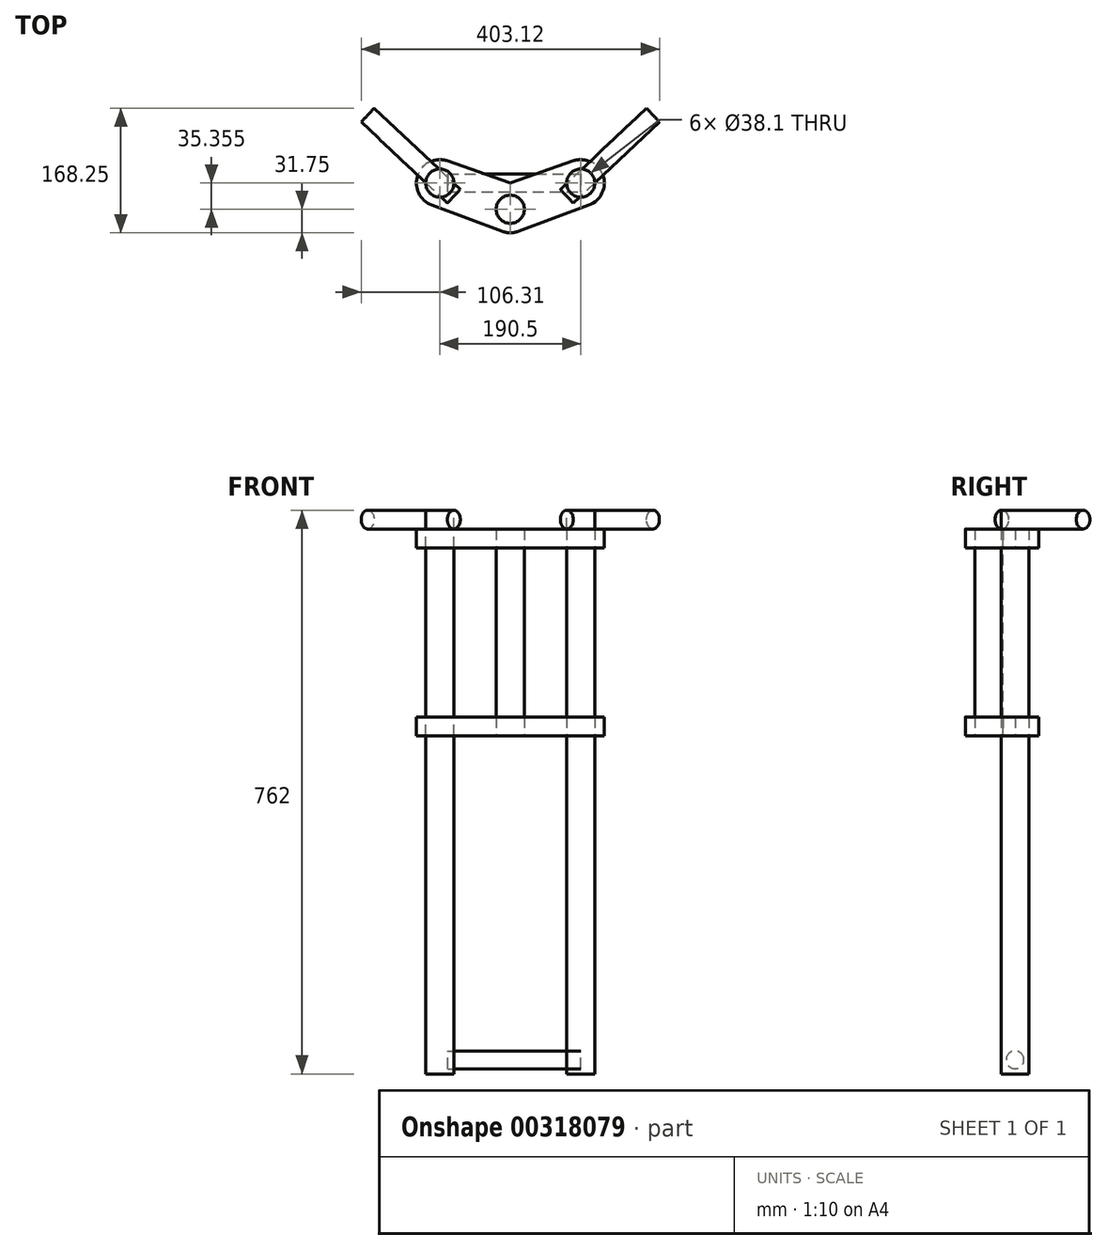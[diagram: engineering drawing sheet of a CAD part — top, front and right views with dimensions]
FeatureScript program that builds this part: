
annotation { "Feature Type Name" : "Feature", "Feature Type Description" : "" }
export const myFeature = defineFeature(function(context is Context, id is Id, definition is map)
    precondition{}
    {
        {
            var Q0;
            Q0=qCreatedBy(makeId("Top.planeOp"),FACE);
            var sketch = newSketch(context, id + "F0", { "sketchPlane" : qUnion([Q0])});
            skCircle(sketch, "E0", {"center": v(0, 0) * mm, "radius": 19.05 * mm});
            skCircle(sketch, "E1", {"center": v(-95.25, 35.36) * mm, "radius": 19.05 * mm});
            skCircle(sketch, "E2", {"center": v(95.25, 35.36) * mm, "radius": 19.05 * mm});
            skCircle(sketch, "E3.0", {"center": v(-95.25, 35.36) * mm, "radius": 31.75 * mm});
            skCircle(sketch, "E4.0", {"center": v(95.25, 35.36) * mm, "radius": 31.75 * mm});
            skCircle(sketch, "E5.0", {"center": v(0, 0) * mm, "radius": 31.75 * mm});
            skLineSegment(sketch, "E6", {"start": v(-106.3, 5.59) * mm, "end": v(-11.05, -29.77) * mm});
            skLineSegment(sketch, "E7", {"start": v(106.3, 5.59) * mm, "end": v(11.05, -29.77) * mm});
            skLineSegment(sketch, "E8", {"start": v(-84.67, 65.29) * mm, "end": v(-2.12, 36.1) * mm});
            skLineSegment(sketch, "E9", {"start": v(84.67, 65.29) * mm, "end": v(2.12, 36.1) * mm});
            skPoint(sketch, "E10.visualSharp", {"position": v(0, 35.36) * mm});
            skArc(sketch, "E10.filletArc", {"start": v(-2.12, 36.1) * mm, "mid": v(0, 35.74) * mm, "end": v(2.12, 36.1) * mm});
            skSolve(sketch);
        }
        {
            var Q0;
            Q0=qCreatedBy(makeId("Top.planeOp"),FACE);
            cPlane(context, id + "F1", {"entities" : qUnion([Q0]), "cplaneType" : CPlaneType.OFFSET, "offset" : 254 * mm, "width" : 152.4 * mm, "height" : 152.4 * mm});
        }
        {
            var Q0;
            Q0=qCreatedBy(id+"F1.planeOp",FACE);
            var sketch = newSketch(context, id + "F2", { "sketchPlane" : qUnion([Q0])});
            skCircle(sketch, "E11.0", {"center": v(0, 0) * mm, "radius": 19.05 * mm});
            skCircle(sketch, "E11.1", {"center": v(-95.25, 35.36) * mm, "radius": 19.05 * mm});
            skCircle(sketch, "E11.2", {"center": v(95.25, 35.36) * mm, "radius": 19.05 * mm});
            skCircle(sketch, "E11.3", {"center": v(-95.25, 35.36) * mm, "radius": 31.75 * mm});
            skCircle(sketch, "E11.4", {"center": v(95.25, 35.36) * mm, "radius": 31.75 * mm});
            skCircle(sketch, "E11.5", {"center": v(0, 0) * mm, "radius": 31.75 * mm});
            skLineSegment(sketch, "E11.6", {"start": v(-106.3, 5.59) * mm, "end": v(-11.05, -29.77) * mm});
            skLineSegment(sketch, "E11.7", {"start": v(106.3, 5.59) * mm, "end": v(11.05, -29.77) * mm});
            skLineSegment(sketch, "E11.8", {"start": v(-84.67, 65.29) * mm, "end": v(-2.12, 36.1) * mm});
            skLineSegment(sketch, "E11.9", {"start": v(84.67, 65.29) * mm, "end": v(2.12, 36.1) * mm});
            skArc(sketch, "E12", {"start": v(-2.12, 36.1) * mm, "mid": v(0, 35.74) * mm, "end": v(2.12, 36.1) * mm});
            skSolve(sketch);
        }
        {
            var Q0;
            Q0 = qSketchRegion(id + "F0", true);
            extrude(context, id + "F3", {"entities" : qUnion([Q0]), "depth" : 25.4 * mm});
        }
        {
            var Q0;
            Q0 = qSketchRegion(id + "F2", true);
            extrude(context, id + "F4", {"entities" : qUnion([Q0]), "depth" : 25.4 * mm});
        }
        {
            var Q0;
            Q0=makeQuery(id+"F0.imprint","IMPRINT",FACE,{"disambiguationData":[TD([[makeQuery(id+"F0.imprint","IMPRINT",EDGE,{"derivedFrom":sQuery(id+"F0.wireOp",EDGE,"E1")}),1.0]])]});
            var Q1;
            Q1=makeQuery(id+"F0.imprint","IMPRINT",FACE,{"disambiguationData":[TD([[makeQuery(id+"F0.imprint","IMPRINT",EDGE,{"derivedFrom":sQuery(id+"F0.wireOp",EDGE,"E2")}),1.0]])]});
            extrude(context, id + "F5", {"entities" : qUnion([Q0, Q1]), "oppositeDirection" : true, "depth" : 457.2 * mm});
        }
        {
            var Q0;
            Q0=makeQuery(id+"F2.imprint","IMPRINT",FACE,{"disambiguationData":[TD([[makeQuery(id+"F2.imprint","IMPRINT",EDGE,{"derivedFrom":sQuery(id+"F2.wireOp",EDGE,"E11.1")}),1.0]])]});
            var Q1;
            Q1=makeQuery(id+"F2.imprint","IMPRINT",FACE,{"disambiguationData":[TD([[makeQuery(id+"F2.imprint","IMPRINT",EDGE,{"derivedFrom":sQuery(id+"F2.wireOp",EDGE,"E11.2")}),1.0]])]});
            extrude(context, id + "F6", {"entities" : qUnion([Q0, Q1]), "endBound" : BoundingType.UP_TO_NEXT, "oppositeDirection" : true, "depth" : 25.4 * mm, "hasSecondDirection" : true, "secondDirectionOppositeDirection" : false, "secondDirectionDepth" : 50.8 * mm});
        }
        {
            var Q0;
            Q0=makeQuery(id+"F2.imprint","IMPRINT",FACE,{"disambiguationData":[TD([[makeQuery(id+"F2.imprint","IMPRINT",EDGE,{"derivedFrom":sQuery(id+"F2.wireOp",EDGE,"E11.0")}),1.0]])]});
            extrude(context, id + "F7", {"entities" : qUnion([Q0]), "oppositeDirection" : true, "depth" : 254 * mm, "hasSecondDirection" : true, "secondDirectionOppositeDirection" : false, "secondDirectionDepth" : 25.4 * mm});
        }
        {
            var Q0;
            Q0=qCreatedBy(id+"F1.planeOp",FACE);
            cPlane(context, id + "F8", {"entities" : qUnion([Q0]), "cplaneType" : CPlaneType.OFFSET, "offset" : 25.4 * mm, "oppositeDirection" : true, "width" : 152.4 * mm, "height" : 152.4 * mm});
        }
        {
            var Q0;
            Q0=qCreatedBy(id+"F8.planeOp",FACE);
            var sketch = newSketch(context, id + "F9", { "sketchPlane" : qUnion([Q0])});
            skCircle(sketch, "E13.0", {"center": v(0, 0) * mm, "radius": 19.05 * mm});
            skCircle(sketch, "E14.0", {"center": v(0, 0) * mm, "radius": 31.75 * mm});
            skLineSegment(sketch, "E15", {"start": v(-29.05, 12.82) * mm, "end": v(-63.5, -65.25) * mm});
            skLineSegment(sketch, "E16", {"start": v(-63.5, -65.25) * mm, "end": v(63.5, -65.25) * mm});
            skLineSegment(sketch, "E17", {"start": v(63.5, -65.25) * mm, "end": v(29.05, 12.82) * mm});
            skPoint(sketch, "E18", {"position": v(0, -65.25) * mm});
            skSolve(sketch);
        }
        {
            var Q0;
            Q0=makeQuery(id+"F5.opExtrude","CAP_EDGE",EDGE,{"disambiguationData":[OSD([sQuery(id+"F0.wireOp",EDGE,"E2")])],"isStart":false});
            cPlane(context, id + "F10", {"entities" : qUnion([Q0]), "cplaneType" : CPlaneType.LINE_ANGLE, "offset" : 25 * mm, "angle" : 0 * degree, "width" : 150 * mm, "height" : 150 * mm});
        }
        {
            var Q0;
            Q0=qCreatedBy(id+"F10.planeOp",FACE);
            var sketch = newSketch(context, id + "F11", { "sketchPlane" : qUnion([Q0])});
            skLineSegment(sketch, "E19", {"start": v(16.3, -457.2) * mm, "end": v(16.3, 0) * mm});
            skLineSegment(sketch, "E20", {"start": v(54.4, 0) * mm, "end": v(54.4, -457.2) * mm});
            skLineSegment(sketch, "E21.0", {"start": v(16.3, -457.2) * mm, "end": v(54.4, -457.2) * mm});
            skLineSegment(sketch, "E22.bottom", {"start": v(16.3, -457.2) * mm, "end": v(54.4, -457.2) * mm, "construction": true});
            skLineSegment(sketch, "E22.top", {"start": v(16.3, -419.1) * mm, "end": v(54.4, -419.1) * mm, "construction": true});
            skLineSegment(sketch, "E22.left", {"start": v(16.3, -457.2) * mm, "end": v(16.3, -419.1) * mm, "construction": true});
            skLineSegment(sketch, "E22.right", {"start": v(54.4, -457.2) * mm, "end": v(54.4, -419.1) * mm, "construction": true});
            skCircle(sketch, "E23", {"center": v(35.36, -438.15) * mm, "radius": 12 * mm});
            skSolve(sketch);
        }
        {
            var Q0;
            Q0 = qSketchRegion(id + "F11", true);
            extrude(context, id + "F12", {"entities" : qUnion([Q0]), "oppositeDirection" : true, "depth" : 180 * mm});
        }
        {
            var Q0;
            Q0=sQuery(id+"F2.wireOp",VERTEX,"E11.7.end");
            var Q1;
            Q1=sQuery(id+"F9.wireOp",VERTEX,"E15.start");
            var Q2;
            Q2=sQuery(id+"F0.wireOp",VERTEX,"E7.end");
            cPlane(context, id + "F13", {"entities" : qUnion([Q0, Q1, Q2]), "cplaneType" : CPlaneType.THREE_POINT, "offset" : 25 * mm, "width" : 150 * mm, "height" : 150 * mm});
        }
        {
            var Q0;
            Q0=sQuery(id+"F2.wireOp",VERTEX,"E11.6.end");
            var Q1;
            Q1=sQuery(id+"F0.wireOp",VERTEX,"E6.end");
            var Q2;
            Q2=sQuery(id+"F9.wireOp",VERTEX,"E17.end");
            cPlane(context, id + "F14", {"entities" : qUnion([Q0, Q1, Q2]), "cplaneType" : CPlaneType.THREE_POINT, "offset" : 25 * mm, "width" : 150 * mm, "height" : 150 * mm});
        }
        {
            var Q0;
            Q0=qCreatedBy(id+"F13.planeOp",FACE);
            var sketch = newSketch(context, id + "F15", { "sketchPlane" : qUnion([Q0])});
            skLineSegment(sketch, "E24", {"start": v(-58.6, 0) * mm, "end": v(-58.6, 304.8) * mm});
            skLineSegment(sketch, "E25.0", {"start": v(-58.6, 304.8) * mm, "end": v(-20.5, 304.8) * mm});
            skLineSegment(sketch, "E26", {"start": v(-20.5, 304.8) * mm, "end": v(-20.5, 0) * mm});
            skLineSegment(sketch, "E27.0", {"start": v(-71.3, 279.4) * mm, "end": v(-10.5, 279.4) * mm});
            skCircle(sketch, "E28", {"center": v(-39.55, 292.1) * mm, "radius": 12.7 * mm});
            skPoint(sketch, "E28.centerSnap0", {"position": v(-39.55, 304.8) * mm});
            skSolve(sketch);
        }
        {
            var Q0;
            Q0=qCreatedBy(id+"F13.planeOp",FACE);
            cPlane(context, id + "F16", {"entities" : qUnion([Q0]), "cplaneType" : CPlaneType.OFFSET, "offset" : 80 * mm, "width" : 150 * mm, "height" : 150 * mm});
        }
        {
            var Q0;
            Q0=qCreatedBy(id+"F14.planeOp",FACE);
            cPlane(context, id + "F17", {"entities" : qUnion([Q0]), "cplaneType" : CPlaneType.OFFSET, "offset" : 80 * mm, "width" : 150 * mm, "height" : 150 * mm});
        }
        {
            var Q0;
            Q0=qCreatedBy(id+"F16.planeOp",FACE);
            var sketch = newSketch(context, id + "F18", { "sketchPlane" : qUnion([Q0])});
            skCircle(sketch, "E29.0", {"center": v(-39.55, 292.1) * mm, "radius": 12.7 * mm});
            skSolve(sketch);
        }
        {
            var Q0;
            Q0 = qSketchRegion(id + "F18", true);
            extrude(context, id + "F19", {"entities" : qUnion([Q0]), "depth" : 160 * mm});
        }
        {
            var Q0;
            Q0=qCreatedBy(id+"F17.planeOp",FACE);
            var sketch = newSketch(context, id + "F20", { "sketchPlane" : qUnion([Q0])});
            skLineSegment(sketch, "E30.0", {"start": v(20.5, 304.8) * mm, "end": v(58.6, 304.8) * mm});
            skLineSegment(sketch, "E31", {"start": v(20.5, 0) * mm, "end": v(20.5, 304.8) * mm});
            skLineSegment(sketch, "E32", {"start": v(58.6, 304.8) * mm, "end": v(58.6, 0) * mm});
            skPoint(sketch, "E33.0", {"position": v(52.14, 279.4) * mm});
            skLineSegment(sketch, "E34.0", {"start": v(10.5, 279.4) * mm, "end": v(71.3, 279.4) * mm});
            skCircle(sketch, "E35", {"center": v(39.55, 292.1) * mm, "radius": 12.7 * mm});
            skPoint(sketch, "E35.centerSnap0", {"position": v(39.55, 304.8) * mm});
            skSolve(sketch);
        }
        {
            var Q0;
            {var subQ0=sQuery(id+"F20.wireOp",EDGE,"E35");var subQ1=makeQuery(id+"F20.imprint","INTERSECT",VERTEX,{"derivedFrom":[sQuery(id+"F20.wireOp",EDGE,"E30.0"),subQ0]});Q0=makeQuery(id+"F20.imprint","IMPRINT",FACE,{"disambiguationData":[TD([[makeQuery(id+"F20.imprint","IMPRINT",EDGE,{"disambiguationData":[TD([[subQ1,-1.0]])],"derivedFrom":subQ0}),1.0]])]});}
            extrude(context, id + "F21", {"entities" : qUnion([Q0]), "depth" : 160 * mm});
        }
    });
